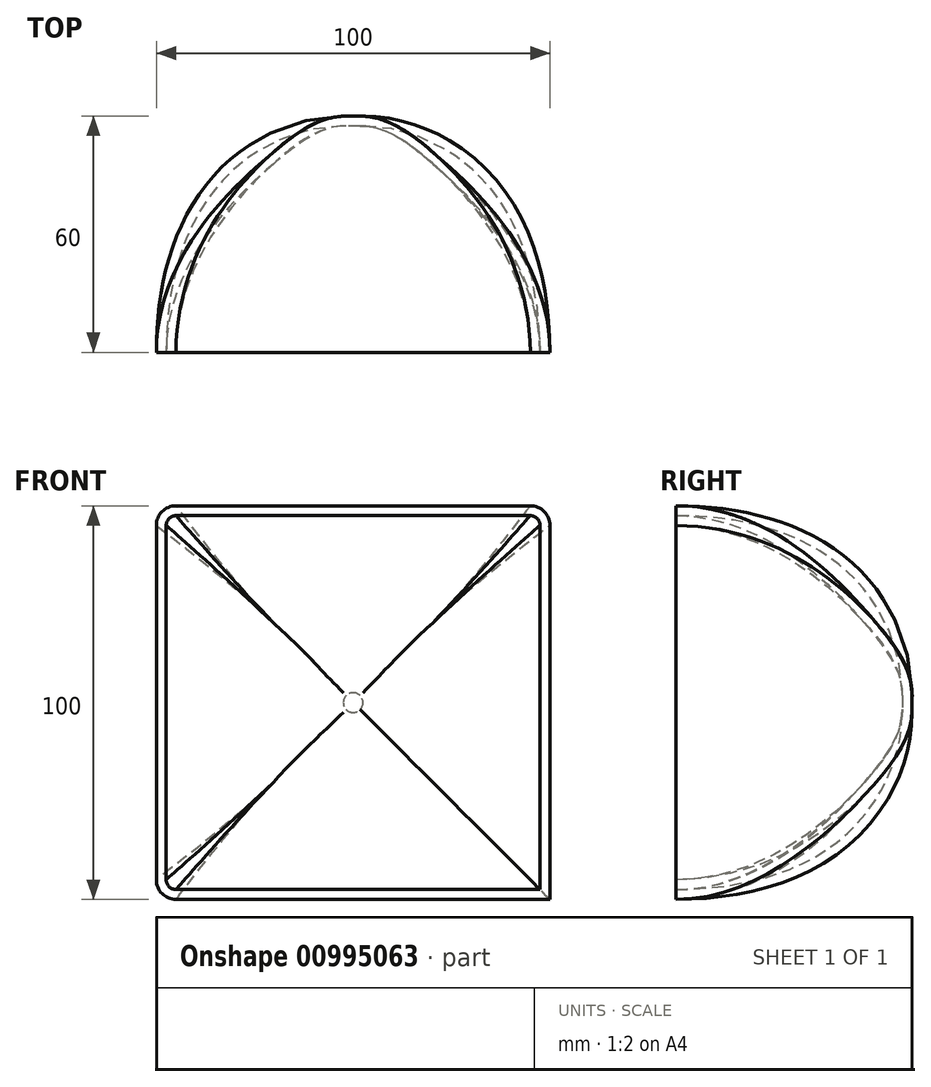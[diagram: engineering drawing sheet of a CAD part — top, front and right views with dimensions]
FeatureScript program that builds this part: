
annotation { "Feature Type Name" : "Feature", "Feature Type Description" : "" }
export const myFeature = defineFeature(function(context is Context, id is Id, definition is map)
    precondition{}
    {
        {
            var Q0;
            Q0=qCreatedBy(makeId("Front.planeOp"),FACE);
            var sketch = newSketch(context, id + "F0", { "sketchPlane" : qUnion([Q0])});
            skLineSegment(sketch, "E0.bottom", {"start": v(50, 50) * mm, "end": v(-50, 50) * mm});
            skLineSegment(sketch, "E0.top", {"start": v(50, -50) * mm, "end": v(-50, -50) * mm});
            skLineSegment(sketch, "E0.left", {"start": v(50, 50) * mm, "end": v(50, -50) * mm});
            skLineSegment(sketch, "E0.right", {"start": v(-50, 50) * mm, "end": v(-50, -50) * mm});
            skPoint(sketch, "E0.middle", {"position": v(0, 0) * mm});
            skSolve(sketch);
        }
        {
            var Q0;
            Q0=qCreatedBy(makeId("Front.planeOp"),FACE);
            cPlane(context, id + "F1", {"entities" : qUnion([Q0]), "cplaneType" : CPlaneType.OFFSET, "offset" : 50 * mm, "oppositeDirection" : true, "width" : 150 * mm, "height" : 150 * mm});
        }
        {
            var Q0;
            Q0=qCreatedBy(id+"F1.planeOp",FACE);
            var sketch = newSketch(context, id + "F2", { "sketchPlane" : qUnion([Q0])});
            skCircle(sketch, "E1", {"center": v(0, 0) * mm, "radius": 30 * mm});
            skLineSegment(sketch, "E2", {"start": v(0, 0) * mm, "end": v(-21.21, 21.21) * mm, "construction": true});
            skLineSegment(sketch, "E3", {"start": v(0, 0) * mm, "end": v(21.21, -21.21) * mm, "construction": true});
            skLineSegment(sketch, "E4", {"start": v(0, 0) * mm, "end": v(-21.21, -21.21) * mm, "construction": true});
            skLineSegment(sketch, "E5", {"start": v(0, 0) * mm, "end": v(21.21, 21.21) * mm, "construction": true});
            skSolve(sketch);
        }
        {
            var Q0;
            Q0=qCreatedBy(id+"F1.planeOp",FACE);
            cPlane(context, id + "F3", {"entities" : qUnion([Q0]), "cplaneType" : CPlaneType.OFFSET, "offset" : 10 * mm, "oppositeDirection" : true, "width" : 150 * mm, "height" : 150 * mm});
        }
        {
            var Q0;
            Q0=qCreatedBy(id+"F3.planeOp",FACE);
            var sketch = newSketch(context, id + "F4", { "sketchPlane" : qUnion([Q0])});
            skCircle(sketch, "E6", {"center": v(0, 0) * mm, "radius": 2.5 * mm});
            skLineSegment(sketch, "E7", {"start": v(0, 0) * mm, "end": v(1.77, 1.77) * mm, "construction": true});
            skLineSegment(sketch, "E8", {"start": v(0, 0) * mm, "end": v(-1.77, 1.77) * mm, "construction": true});
            skLineSegment(sketch, "E9", {"start": v(0, 0) * mm, "end": v(-1.77, -1.77) * mm, "construction": true});
            skLineSegment(sketch, "E10", {"start": v(0, 0) * mm, "end": v(1.77, -1.77) * mm, "construction": true});
            skSolve(sketch);
        }
        {
            var Q0;
            Q0=makeQuery(id+"F0.imprint","IMPRINT",FACE,{"disambiguationData":[TD([[makeQuery(id+"F0.imprint","IMPRINT",EDGE,{"derivedFrom":sQuery(id+"F0.wireOp",EDGE,"E0.bottom")}),1.0]])]});
            var Q1;
            Q1=makeQuery(id+"F2.imprint","IMPRINT",FACE,{"disambiguationData":[TD([[makeQuery(id+"F2.imprint","IMPRINT",EDGE,{"derivedFrom":sQuery(id+"F2.wireOp",EDGE,"E1")}),1.0]])]});
            var Q2;
            Q2=makeQuery(id+"F4.imprint","IMPRINT",FACE,{"disambiguationData":[TD([[makeQuery(id+"F4.imprint","IMPRINT",EDGE,{"derivedFrom":sQuery(id+"F4.wireOp",EDGE,"E6")}),1.0]])]});
            loft(context, id + "F5", {"startCondition" : LoftEndDerivativeType.NORMAL_TO_PROFILE, "startMagnitude" : 1, "endCondition" : LoftEndDerivativeType.TANGENT_TO_PROFILE, "endMagnitude" : 1, "sheetProfilesArray" : [{ "sheetProfileEntities" : qUnion([Q0]) }, { "sheetProfileEntities" : qUnion([Q1]) }, { "sheetProfileEntities" : qUnion([Q2]) }]});
        }
        {
            var Q0;
            Q0=makeQuery(id+"F5.opLoft","SWEPT_EDGE",EDGE,{"disambiguationData":[OSD([sQuery(id+"F0.wireOp",EDGE,"E0.bottom"),sQuery(id+"F0.wireOp",EDGE,"E0.top"),sQuery(id+"F0.wireOp",EDGE,"E0.left"),sQuery(id+"F2.wireOp",EDGE,"E1"),sQuery(id+"F4.wireOp",EDGE,"E6")])]});
            var Q1;
            Q1=makeQuery(id+"F5.opLoft","SWEPT_EDGE",EDGE,{"disambiguationData":[OSD([sQuery(id+"F0.wireOp",EDGE,"E0.top"),sQuery(id+"F0.wireOp",EDGE,"E0.left"),sQuery(id+"F0.wireOp",EDGE,"E0.right"),sQuery(id+"F2.wireOp",EDGE,"E1"),sQuery(id+"F4.wireOp",EDGE,"E6")])]});
            var Q2;
            Q2=makeQuery(id+"F5.opLoft","SWEPT_EDGE",EDGE,{"disambiguationData":[OSD([sQuery(id+"F0.wireOp",EDGE,"E0.bottom"),sQuery(id+"F0.wireOp",EDGE,"E0.left")])]});
            var Q3;
            Q3=makeQuery(id+"F5.opLoft","SWEPT_EDGE",EDGE,{"disambiguationData":[OSD([sQuery(id+"F0.wireOp",EDGE,"E0.bottom"),sQuery(id+"F0.wireOp",EDGE,"E0.top"),sQuery(id+"F0.wireOp",EDGE,"E0.right"),sQuery(id+"F2.wireOp",EDGE,"E1"),sQuery(id+"F4.wireOp",EDGE,"E6")])]});
            fillet(context, id + "F6", {"entities" : qUnion([Q0, Q1, Q2, Q3]), "radius" : 5 * mm, "tangentPropagation" : true, "allowEdgeOverflow" : false});
        }
        {
            var Q0;
            Q0=makeQuery(id+"F5.opLoft","CAP_FACE",FACE,{"disambiguationData":[OSD([makeQuery(id+"F0.imprint","IMPRINT",FACE,{"disambiguationData":[TD([[makeQuery(id+"F0.imprint","IMPRINT",EDGE,{"derivedFrom":sQuery(id+"F0.wireOp",EDGE,"E0.bottom")}),1.0]])]})])],"isStart":true});
            shell(context, id + "F7", {"entities" : qUnion([Q0]), "thickness" : 2.5 * mm});
        }
    });
